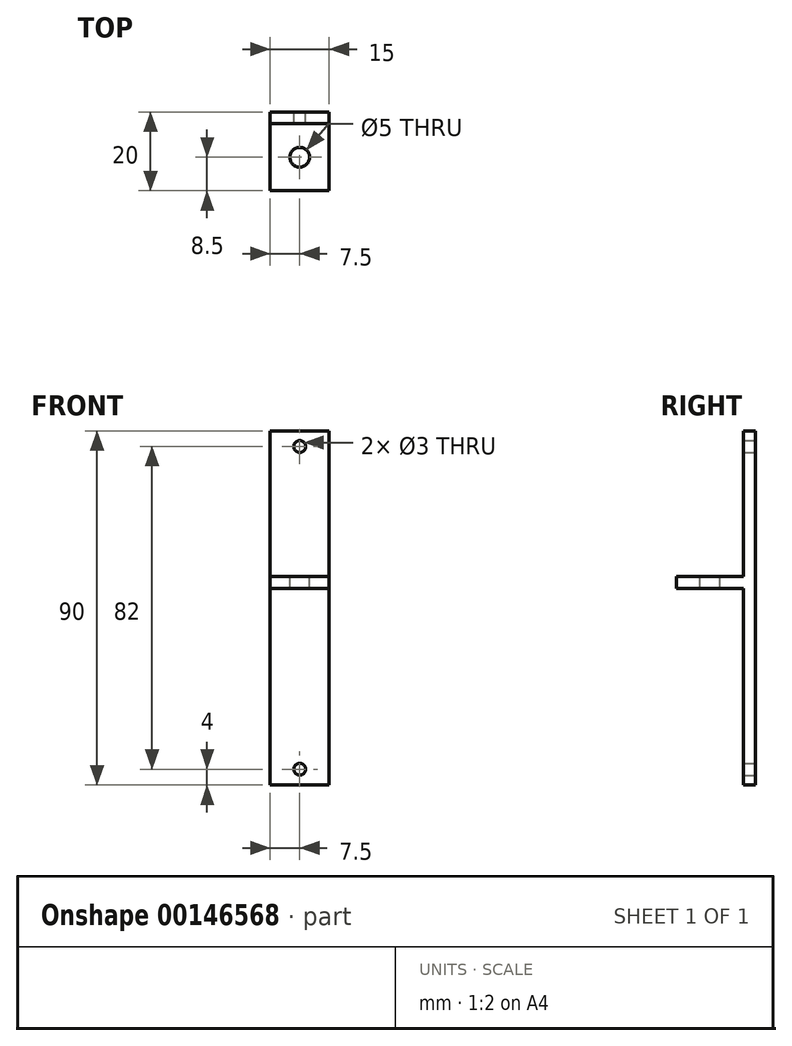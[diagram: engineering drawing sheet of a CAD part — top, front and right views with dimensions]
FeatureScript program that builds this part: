
annotation { "Feature Type Name" : "Feature", "Feature Type Description" : "" }
export const myFeature = defineFeature(function(context is Context, id is Id, definition is map)
    precondition{}
    {
        {
            var Q0;
            Q0=qCreatedBy(makeId("Front.planeOp"),FACE);
            var sketch = newSketch(context, id + "F0", { "sketchPlane" : qUnion([Q0])});
            skLineSegment(sketch, "E0.bottom", {"start": v(7.5, -45) * mm, "end": v(-7.5, -45) * mm});
            skLineSegment(sketch, "E0.top", {"start": v(7.5, 45) * mm, "end": v(-7.5, 45) * mm});
            skLineSegment(sketch, "E0.left", {"start": v(7.5, -45) * mm, "end": v(7.5, 45) * mm});
            skLineSegment(sketch, "E0.right", {"start": v(-7.5, -45) * mm, "end": v(-7.5, 45) * mm});
            skPoint(sketch, "E0.middle", {"position": v(0, 0) * mm});
            skLineSegment(sketch, "E1", {"start": v(0, 45) * mm, "end": v(0, -45) * mm, "construction": true});
            skLineSegment(sketch, "E2", {"start": v(-7.5, 5) * mm, "end": v(7.5, 5) * mm, "construction": true});
            skCircle(sketch, "E3", {"center": v(0, 41) * mm, "radius": 1.5 * mm});
            skCircle(sketch, "E4", {"center": v(0, -41) * mm, "radius": 1.5 * mm});
            skSolve(sketch);
        }
        {
            var Q0;
            Q0 = qSketchRegion(id + "F0", true);
            extrude(context, id + "F1", {"entities" : qUnion([Q0]), "depth" : 3 * mm});
        }
        {
            var Q0;
            Q0=makeQuery(id+"F1.opExtrude","CAP_FACE",FACE,{"disambiguationData":[OSD([sQuery(id+"F0.wireOp",EDGE,"E0.bottom"),sQuery(id+"F0.wireOp",EDGE,"E0.top"),sQuery(id+"F0.wireOp",EDGE,"E0.left"),sQuery(id+"F0.wireOp",EDGE,"E0.right"),sQuery(id+"F0.wireOp",EDGE,"E3"),sQuery(id+"F0.wireOp",EDGE,"E4")])],"isStart":false});
            var sketch = newSketch(context, id + "F2", { "sketchPlane" : qUnion([Q0])});
            skLineSegment(sketch, "E5.bottom", {"start": v(7.5, 8) * mm, "end": v(-7.5, 8) * mm});
            skLineSegment(sketch, "E5.top", {"start": v(7.5, 5) * mm, "end": v(-7.5, 5) * mm});
            skLineSegment(sketch, "E5.left", {"start": v(7.5, 8) * mm, "end": v(7.5, 5) * mm});
            skLineSegment(sketch, "E5.right", {"start": v(-7.5, 8) * mm, "end": v(-7.5, 5) * mm});
            skPoint(sketch, "E5.middle", {"position": v(0, 6.5) * mm});
            skSolve(sketch);
        }
        {
            var Q0;
            Q0 = qSketchRegion(id + "F2", true);
            extrude(context, id + "F3", {"entities" : qUnion([Q0]), "operationType" : NewBodyOperationType.ADD, "depth" : 17 * mm});
        }
        {
            var Q0;
            Q0=makeQuery(id+"F3.opExtrude","SWEPT_FACE",FACE,{"disambiguationData":[OSD([sQuery(id+"F2.wireOp",EDGE,"E5.bottom")])]});
            var sketch = newSketch(context, id + "F4", { "sketchPlane" : qUnion([Q0])});
            skLineSegment(sketch, "E6", {"start": v(-7.5, -11.5) * mm, "end": v(7.5, -11.5) * mm, "construction": true});
            skLineSegment(sketch, "E7", {"start": v(0, -20) * mm, "end": v(0, 0) * mm, "construction": true});
            skCircle(sketch, "E8", {"center": v(0, -11.5) * mm, "radius": 2.5 * mm});
            skSolve(sketch);
        }
        {
            var Q0;
            Q0 = qSketchRegion(id + "F4", true);
            extrude(context, id + "F5", {"entities" : qUnion([Q0]), "operationType" : NewBodyOperationType.REMOVE, "endBound" : BoundingType.THROUGH_ALL, "oppositeDirection" : true, "depth" : 25 * mm});
        }
    });
